# Revit family: Furniture_Office-Chairs_Flokk_HAG_Tion_2100
name_source: partatom
category: Furniture
revit_build: Autodesk Revit 2018 (Build: 20170223_1515(x64)
units: mm (PartAtom-declared; Revit-internal decimal feet)

## family parameters
Always vertical = Yes
Cut with Voids When Loaded = No
OmniClass Number = 23.40.20.14.14.11
OmniClass Title = Chairs
Room Calculation Point = No
Shared = No
Work Plane-Based = No

## types (2) — shared parameters
AssetType = Movable
BIMObjectName = Furniture_Office-Chairs_Flokk_HAG_Tion_2100
Brand = HAG
Category = Office Chair
Collection = HAG
Color = Various
DurationUnit = Year
Features = Adjustable seat height and depth, adjustable back height and angle
HighestSeatingHeight = 485 mm  [stored 1.59121 ft]
IfcExportAs = IfcFurnishingElementType
IfcExportType = CHAIR
LowestSeatingHeight = 400 mm  [stored 1.31234 ft]
MainColor = Various
Manufacturer = Flokk
ManufacturerName = Flokk
ManufacturerURL = https://www.flokk.com
Material = Textile, metal, plastic
NBSDescription = Office chairs
NBSReference = 45-35-20/330
Name = HAG_Tion_2100
NominalDepth = 592 mm
NominalLength = 619 mm
OfficeChairTertiaryMaterial = Plastic, Opaque Black
ProductInformation = n/a
adapted to your height and weight.
Shape = Sculptured
Size = 600x600x710/860 mm
Uniclass2 = Pr_40_50_12_57
Uniclass2015Description = Office chairs
Uniclass2015Reference = Pr_40_50_12_57
Version = 1
VersionDate = 28/11/2021
WarrantyDurationUnit = Year
zero-valued in all types: Cost

## per-type parameters (varying)
| type | Model | OfficeChairMainMaterial | OfficeChairSecondaryMaterial |
| 2100 - without armrests Moss | 2100 | Moss RAL 6013 | Moss grey NCS S7010 G50Y |
| 2100 - without armrests Chestnut | BMA Axia 2.1 | Chestnut RAL 8015 | Blush rose RAL 0405030 |

note: [stored X ft] marks values corroborated as IEEE doubles in the binary element streams (Revit-internal decimal feet)

## geometry (parser evidence)
native form markers: Sweep x14
no freeform markers — native parametric forms only
